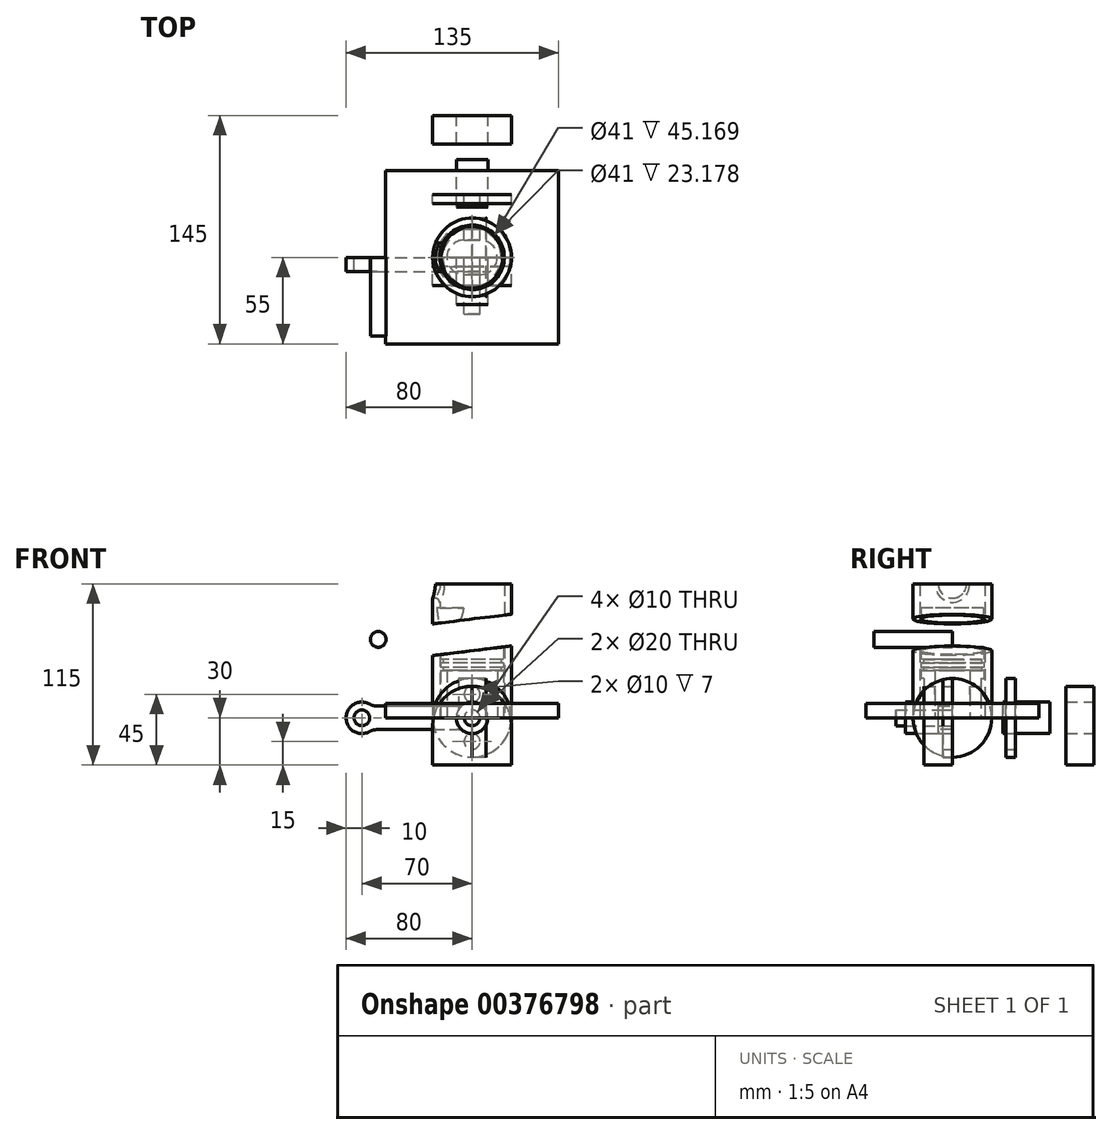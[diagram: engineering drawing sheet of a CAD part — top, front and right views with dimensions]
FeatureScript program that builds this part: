
annotation { "Feature Type Name" : "Feature", "Feature Type Description" : "" }
export const myFeature = defineFeature(function(context is Context, id is Id, definition is map)
    precondition{}
    {
        {
            var Q0;
            Q0=qCreatedBy(makeId("Front.planeOp"),FACE);
            var sketch = newSketch(context, id + "F0", { "sketchPlane" : qUnion([Q0])});
            skCircle(sketch, "E0", {"center": v(0, 0) * mm, "radius": 25 * mm});
            skCircle(sketch, "E1", {"center": v(0, -15) * mm, "radius": 5 * mm});
            skSolve(sketch);
        }
        {
            var Q0;
            Q0 = qSketchRegion(id + "F0", true);
            extrude(context, id + "F1", {"entities" : qUnion([Q0]), "depth" : 6 * mm});
        }
        {
            var Q0;
            Q0=makeQuery(id+"F1.opExtrude","SWEPT_BODY",BODY,{"disambiguationData":[OSD([sQuery(id+"F0.wireOp",EDGE,"E0"),sQuery(id+"F0.wireOp",EDGE,"E1")])]});
            transform(context, id + "F2", {"entities" : qUnion([Q0]), "transformType" : TransformType.TRANSLATION_3D, "dx" : 0 * mm, "dy" : 40 * mm, "dz" : 0 * mm, "makeCopy" : true});
        }
        {
            var Q0;
            Q0=qCreatedBy(makeId("Front.planeOp"),FACE);
            var sketch = newSketch(context, id + "F3", { "sketchPlane" : qUnion([Q0])});
            skCircle(sketch, "E2", {"center": v(-59.58, 49.8) * mm, "radius": 5 * mm});
            skSolve(sketch);
        }
        {
            var Q0;
            Q0=makeQuery(id+"F3.imprint","IMPRINT",FACE,{"disambiguationData":[TD([[makeQuery(id+"F3.imprint","IMPRINT",EDGE,{"derivedFrom":sQuery(id+"F3.wireOp",EDGE,"E2")}),1.0]])]});
            extrude(context, id + "F4", {"entities" : qUnion([Q0]), "depth" : 50 * mm});
        }
        {
            var Q0;
            Q0=qCreatedBy(makeId("Front.planeOp"),FACE);
            var sketch = newSketch(context, id + "F5", { "sketchPlane" : qUnion([Q0])});
            skCircle(sketch, "E3", {"center": v(0, 0) * mm, "radius": 10 * mm});
            skCircle(sketch, "E4", {"center": v(-70, 0) * mm, "radius": 10 * mm});
            skLineSegment(sketch, "E5", {"start": v(-70, 0) * mm, "end": v(0, 0) * mm, "construction": true});
            skLineSegment(sketch, "E6", {"start": v(-63.39, 7.5) * mm, "end": v(-6.61, 7.5) * mm});
            skLineSegment(sketch, "E7.MirrorCS", {"start": v(-63.39, -7.5) * mm, "end": v(-6.61, -7.5) * mm});
            skCircle(sketch, "E8", {"center": v(-70, 0) * mm, "radius": 5 * mm});
            skCircle(sketch, "E9", {"center": v(0, 0) * mm, "radius": 5 * mm});
            skSolve(sketch);
        }
        {
            var Q0;
            Q0 = qSketchRegion(id + "F5", true);
            extrude(context, id + "F6", {"entities" : qUnion([Q0]), "depth" : 9 * mm});
        }
        {
            var Q0;
            Q0=makeQuery(id+"F6.opExtrude","SWEPT_EDGE",EDGE,{"disambiguationData":[OSD([sQuery(id+"F5.wireOp",EDGE,"E4"),sQuery(id+"F5.wireOp",EDGE,"E6")])]});
            var Q1;
            Q1=makeQuery(id+"F6.opExtrude","SWEPT_EDGE",EDGE,{"disambiguationData":[OSD([sQuery(id+"F5.wireOp",EDGE,"E4"),sQuery(id+"F5.wireOp",EDGE,"E7.MirrorCS")])]});
            fillet(context, id + "F7", {"entities" : qUnion([Q0, Q1]), "radius" : 10 * mm, "tangentPropagation" : true, "allowEdgeOverflow" : false});
        }
        {
            var Q0;
            Q0=makeQuery(id+"F6.opExtrude","SWEPT_EDGE",EDGE,{"disambiguationData":[OSD([sQuery(id+"F5.wireOp",EDGE,"E3"),sQuery(id+"F5.wireOp",EDGE,"E6")])]});
            var Q1;
            Q1=makeQuery(id+"F6.opExtrude","SWEPT_EDGE",EDGE,{"disambiguationData":[OSD([sQuery(id+"F5.wireOp",EDGE,"E3"),sQuery(id+"F5.wireOp",EDGE,"E7.MirrorCS")])]});
            fillet(context, id + "F8", {"entities" : qUnion([Q0, Q1]), "radius" : 10 * mm, "tangentPropagation" : true, "allowEdgeOverflow" : false});
        }
        {
            var Q0;
            Q0=qCreatedBy(makeId("Top.planeOp"),FACE);
            var sketch = newSketch(context, id + "F9", { "sketchPlane" : qUnion([Q0])});
            skCircle(sketch, "E10", {"center": v(0, 0) * mm, "radius": 20 * mm});
            skSolve(sketch);
        }
        {
            var Q0;
            Q0 = qSketchRegion(id + "F9", true);
            extrude(context, id + "F10", {"entities" : qUnion([Q0]), "depth" : 40 * mm});
        }
        {
            var Q0;
            Q0=qCreatedBy(makeId("Top.planeOp"),FACE);
            var sketch = newSketch(context, id + "F11", { "sketchPlane" : qUnion([Q0])});
            skCircle(sketch, "E11", {"center": v(0, 0) * mm, "radius": 11 * mm});
            skCircle(sketch, "E12", {"center": v(10, 0) * mm, "radius": 11 * mm});
            skLineSegment(sketch, "E13", {"start": v(0, -11) * mm, "end": v(10, -11) * mm});
            skLineSegment(sketch, "E14.MirrorCS", {"start": v(0, 11) * mm, "end": v(10, 11) * mm});
            skSolve(sketch);
        }
        {
            var Q0;
            {var subQ0=sQuery(id+"F11.wireOp",EDGE,"E14.MirrorCS");Q0=makeQuery(id+"F11.imprint","IMPRINT",FACE,{"disambiguationData":[TD([[makeQuery(id+"F11.imprint","IMPRINT",EDGE,{"derivedFrom":subQ0}),-1.0]])]});}
            var Q1;
            {var subQ0=sQuery(id+"F11.wireOp",EDGE,"E13");Q1=makeQuery(id+"F11.imprint","IMPRINT",FACE,{"disambiguationData":[TD([[makeQuery(id+"F11.imprint","IMPRINT",EDGE,{"derivedFrom":subQ0}),1.0]])]});}
            var Q2;
            {var subQ0=sQuery(id+"F11.wireOp",EDGE,"E12");var subQ1=sQuery(id+"F11.wireOp",EDGE,"E11");var subQ2=makeQuery(id+"F11.imprint","INTERSECT",VERTEX,{"disambiguationData":[OD(0.0)],"derivedFrom":[subQ1,subQ0]});Q2=makeQuery(id+"F11.imprint","IMPRINT",FACE,{"disambiguationData":[TD([[makeQuery(id+"F11.imprint","IMPRINT",EDGE,{"disambiguationData":[TD([[subQ2,1.0]])],"derivedFrom":subQ1}),1.0]])]});}
            var Q3;
            {var subQ0=sQuery(id+"F11.wireOp",EDGE,"E12");var subQ1=sQuery(id+"F11.wireOp",EDGE,"E11");var subQ2=makeQuery(id+"F11.imprint","INTERSECT",VERTEX,{"disambiguationData":[OD(0.0)],"derivedFrom":[subQ1,subQ0]});Q3=makeQuery(id+"F11.imprint","IMPRINT",FACE,{"disambiguationData":[TD([[makeQuery(id+"F11.imprint","IMPRINT",EDGE,{"disambiguationData":[TD([[subQ2,1.0]])],"derivedFrom":subQ1}),-1.0]])]});}
            var Q4;
            {var subQ0=sQuery(id+"F11.wireOp",EDGE,"E11");var subQ1=makeQuery(id+"F11.imprint","INTERSECT",VERTEX,{"derivedFrom":[subQ0,sQuery(id+"F11.wireOp",EDGE,"E14.MirrorCS")]});Q4=makeQuery(id+"F11.imprint","IMPRINT",FACE,{"disambiguationData":[TD([[makeQuery(id+"F11.imprint","IMPRINT",EDGE,{"disambiguationData":[TD([[subQ1,1.0]])],"derivedFrom":subQ0}),1.0]])]});}
            extrude(context, id + "F12", {"entities" : qUnion([Q0, Q1, Q2, Q3, Q4]), "depth" : 30 * mm});
        }
        {
            var Q0;
            Q0=makeQuery(id+"F12.opExtrude","SWEPT_BODY",BODY,{"disambiguationData":[OSD([sQuery(id+"F11.wireOp",EDGE,"E11"),sQuery(id+"F11.wireOp",EDGE,"E12"),sQuery(id+"F11.wireOp",EDGE,"E13"),sQuery(id+"F11.wireOp",EDGE,"E14.MirrorCS")])]});
            var Q1;
            Q1=qCreatedBy(makeId("Right.planeOp"),FACE);
            transform(context, id + "F13", {"entities" : qUnion([Q0]), "transformType" : TransformType.TRANSLATION_DISTANCE, "transformDirection" : qUnion([Q1]), "distance" : 5 * mm, "oppositeDirection" : true, "makeCopy" : false});
        }
        {
            var Q0;
            Q0=makeQuery(id+"F12.opExtrude","SWEPT_BODY",BODY,{"disambiguationData":[OSD([sQuery(id+"F11.wireOp",EDGE,"E11"),sQuery(id+"F11.wireOp",EDGE,"E12"),sQuery(id+"F11.wireOp",EDGE,"E13"),sQuery(id+"F11.wireOp",EDGE,"E14.MirrorCS")])]});
            var Q1;
            Q1=makeQuery(id+"F10.opExtrude","SWEPT_BODY",BODY,{"disambiguationData":[OSD([sQuery(id+"F9.wireOp",EDGE,"E10")])]});
            booleanBodies(context, id + "F14", {"operationType" : BooleanOperationType.SUBTRACTION, "tools" : qUnion([Q0]), "targets" : qUnion([Q1])});
        }
        {
            var Q0;
            Q0=qCreatedBy(makeId("Top.planeOp"),FACE);
            var sketch = newSketch(context, id + "F15", { "sketchPlane" : qUnion([Q0])});
            skLineSegment(sketch, "E15.bottom", {"start": v(-45, 18) * mm, "end": v(45, 18) * mm});
            skLineSegment(sketch, "E15.top", {"start": v(-45, -18) * mm, "end": v(45, -18) * mm});
            skLineSegment(sketch, "E15.left", {"start": v(-45, 18) * mm, "end": v(-45, -18) * mm});
            skLineSegment(sketch, "E15.right", {"start": v(45, 18) * mm, "end": v(45, -18) * mm});
            skPoint(sketch, "E15.middle", {"position": v(0, 0) * mm});
            skSolve(sketch);
        }
        {
            var Q0;
            Q0 = qSketchRegion(id + "F15", true);
            extrude(context, id + "F16", {"entities" : qUnion([Q0]), "depth" : 35 * mm});
        }
        {
            var Q0;
            Q0=qCreatedBy(makeId("Top.planeOp"),FACE);
            var sketch = newSketch(context, id + "F17", { "sketchPlane" : qUnion([Q0])});
            skLineSegment(sketch, "E16.bottom", {"start": v(-50, 23) * mm, "end": v(50, 23) * mm});
            skLineSegment(sketch, "E16.top", {"start": v(-50, -23) * mm, "end": v(50, -23) * mm});
            skLineSegment(sketch, "E16.left", {"start": v(-50, 23) * mm, "end": v(-50, -23) * mm});
            skLineSegment(sketch, "E16.right", {"start": v(50, 23) * mm, "end": v(50, -23) * mm});
            skPoint(sketch, "E16.middle", {"position": v(0, 0) * mm});
            skSolve(sketch);
        }
        {
            var Q0;
            Q0 = qSketchRegion(id + "F17", true);
            extrude(context, id + "F18", {"entities" : qUnion([Q0]), "depth" : 25 * mm});
        }
        {
            var Q0;
            Q0=makeQuery(id+"F16.opExtrude","SWEPT_BODY",BODY,{"disambiguationData":[OSD([sQuery(id+"F15.wireOp",EDGE,"E15.bottom"),sQuery(id+"F15.wireOp",EDGE,"E15.top"),sQuery(id+"F15.wireOp",EDGE,"E15.left"),sQuery(id+"F15.wireOp",EDGE,"E15.right")])]});
            var Q1;
            Q1=makeQuery(id+"F18.opExtrude","SWEPT_BODY",BODY,{"disambiguationData":[OSD([sQuery(id+"F17.wireOp",EDGE,"E16.bottom"),sQuery(id+"F17.wireOp",EDGE,"E16.top"),sQuery(id+"F17.wireOp",EDGE,"E16.left"),sQuery(id+"F17.wireOp",EDGE,"E16.right")])]});
            booleanBodies(context, id + "F19", {"operationType" : BooleanOperationType.SUBTRACTION, "tools" : qUnion([Q0]), "targets" : qUnion([Q1])});
        }
        {
            var Q0;
            Q0=makeQuery(id+"F18.opExtrude","SWEPT_BODY",BODY,{"disambiguationData":[OSD([sQuery(id+"F17.wireOp",EDGE,"E16.bottom"),sQuery(id+"F17.wireOp",EDGE,"E16.top"),sQuery(id+"F17.wireOp",EDGE,"E16.left"),sQuery(id+"F17.wireOp",EDGE,"E16.right")])]});
            var Q1;
            Q1=makeQuery(id+"F10.opExtrude","SWEPT_BODY",BODY,{"disambiguationData":[OSD([sQuery(id+"F9.wireOp",EDGE,"E10")])]});
            booleanBodies(context, id + "F20", {"operationType" : BooleanOperationType.SUBTRACTION, "tools" : qUnion([Q0]), "targets" : qUnion([Q1])});
        }
        {
            var Q0;
            Q0=makeQuery(id+"F20.opBoolean","COPY",FACE,{"derivedFrom":makeQuery(id+"F19.opBoolean","COPY",FACE,{"derivedFrom":makeQuery(id+"F16.opExtrude","SWEPT_FACE",FACE,{"disambiguationData":[OSD([sQuery(id+"F15.wireOp",EDGE,"E15.top")])]})})});
            var sketch = newSketch(context, id + "F21", { "sketchPlane" : qUnion([Q0])});
            skCircle(sketch, "E17", {"center": v(0, 15) * mm, "radius": 5 * mm});
            skSolve(sketch);
        }
        {
            var Q0;
            Q0=makeQuery(id+"F21.imprint","IMPRINT",FACE,{"disambiguationData":[TD([[makeQuery(id+"F21.imprint","IMPRINT",EDGE,{"derivedFrom":sQuery(id+"F21.wireOp",EDGE,"E17")}),1.0]])]});
            extrude(context, id + "F22", {"entities" : qUnion([Q0]), "depth" : 45 * mm});
        }
        {
            var Q0;
            Q0=makeQuery(id+"F22.opExtrude","SWEPT_BODY",BODY,{"disambiguationData":[OSD([sQuery(id+"F21.wireOp",EDGE,"E17")])]});
            var Q1;
            Q1=qCreatedBy(makeId("Front.planeOp"),FACE);
            transform(context, id + "F23", {"entities" : qUnion([Q0]), "transformType" : TransformType.TRANSLATION_DISTANCE, "transformDirection" : qUnion([Q1]), "distance" : 41 * mm, "oppositeDirection" : true, "makeCopy" : false});
        }
        {
            var Q0;
            Q0=makeQuery(id+"F22.opExtrude","SWEPT_BODY",BODY,{"disambiguationData":[OSD([sQuery(id+"F21.wireOp",EDGE,"E17")])]});
            var Q1;
            Q1=makeQuery(id+"F10.opExtrude","SWEPT_BODY",BODY,{"disambiguationData":[OSD([sQuery(id+"F9.wireOp",EDGE,"E10")])]});
            booleanBodies(context, id + "F24", {"operationType" : BooleanOperationType.SUBTRACTION, "tools" : qUnion([Q0]), "targets" : qUnion([Q1])});
        }
        {
            var Q0;
            Q0=qCreatedBy(makeId("Top.planeOp"),FACE);
            var sketch = newSketch(context, id + "F25", { "sketchPlane" : qUnion([Q0])});
            skCircle(sketch, "E18", {"center": v(0, 0) * mm, "radius": 25 * mm});
            skCircle(sketch, "E19", {"center": v(0, 0) * mm, "radius": 18.5 * mm});
            skSolve(sketch);
        }
        {
            var Q0;
            Q0 = qSketchRegion(id + "F25", true);
            extrude(context, id + "F26", {"entities" : qUnion([Q0]), "depth" : 2 * mm});
        }
        {
            var Q0;
            Q0=makeQuery(id+"F26.opExtrude","SWEPT_BODY",BODY,{"disambiguationData":[OSD([sQuery(id+"F25.wireOp",EDGE,"E18"),sQuery(id+"F25.wireOp",EDGE,"E19")])]});
            var Q1;
            Q1=qCreatedBy(makeId("Top.planeOp"),FACE);
            transform(context, id + "F27", {"entities" : qUnion([Q0]), "transformType" : TransformType.TRANSLATION_DISTANCE, "transformDirection" : qUnion([Q1]), "distance" : 30 * mm, "makeCopy" : false});
        }
        {
            var Q0;
            Q0=makeQuery(id+"F26.opExtrude","SWEPT_BODY",BODY,{"disambiguationData":[OSD([sQuery(id+"F25.wireOp",EDGE,"E18"),sQuery(id+"F25.wireOp",EDGE,"E19")])]});
            transform(context, id + "F28", {"entities" : qUnion([Q0]), "transformType" : TransformType.TRANSLATION_3D, "dx" : 0 * mm, "dy" : 0 * mm, "dz" : 5 * mm, "makeCopy" : true});
        }
        {
            var Q0;
            Q0=makeQuery(id+"F28.opPattern","COPY",BODY,{"derivedFrom":makeQuery(id+"F26.opExtrude","SWEPT_BODY",BODY,{"disambiguationData":[OSD([sQuery(id+"F25.wireOp",EDGE,"E18"),sQuery(id+"F25.wireOp",EDGE,"E19")])]}),"instanceName":"1"});
            var Q1;
            Q1=makeQuery(id+"F26.opExtrude","SWEPT_BODY",BODY,{"disambiguationData":[OSD([sQuery(id+"F25.wireOp",EDGE,"E18"),sQuery(id+"F25.wireOp",EDGE,"E19")])]});
            var Q2;
            Q2=makeQuery(id+"F10.opExtrude","SWEPT_BODY",BODY,{"disambiguationData":[OSD([sQuery(id+"F9.wireOp",EDGE,"E10")])]});
            booleanBodies(context, id + "F29", {"operationType" : BooleanOperationType.SUBTRACTION, "tools" : qUnion([Q0, Q1]), "targets" : qUnion([Q2])});
        }
        {
            var Q0;
            Q0=qCreatedBy(makeId("Front.planeOp"),FACE);
            var sketch = newSketch(context, id + "F30", { "sketchPlane" : qUnion([Q0])});
            skCircle(sketch, "E20", {"center": v(0, 0) * mm, "radius": 5 * mm});
            skSolve(sketch);
        }
        {
            var Q0;
            Q0 = qSketchRegion(id + "F30", true);
            extrude(context, id + "F31", {"entities" : qUnion([Q0]), "depth" : 36 * mm});
        }
        {
            var Q0;
            Q0=qCreatedBy(makeId("Top.planeOp"),FACE);
            var sketch = newSketch(context, id + "F32", { "sketchPlane" : qUnion([Q0])});
            skCircle(sketch, "E21", {"center": v(0, 0) * mm, "radius": 25 * mm});
            skCircle(sketch, "E22", {"center": v(0, 0) * mm, "radius": 20.5 * mm});
            skSolve(sketch);
        }
        {
            var Q0;
            Q0 = qSketchRegion(id + "F32", true);
            extrude(context, id + "F33", {"entities" : qUnion([Q0]), "depth" : 85 * mm});
        }
        {
            var Q0;
            Q0=qCreatedBy(makeId("Front.planeOp"),FACE);
            var sketch = newSketch(context, id + "F34", { "sketchPlane" : qUnion([Q0])});
            skCircle(sketch, "E23", {"center": v(0, 0) * mm, "radius": 10 * mm});
            skSolve(sketch);
        }
        {
            var Q0;
            Q0=makeQuery(id+"F34.imprint","IMPRINT",FACE,{"disambiguationData":[TD([[makeQuery(id+"F34.imprint","IMPRINT",EDGE,{"derivedFrom":sQuery(id+"F34.wireOp",EDGE,"E23")}),1.0]])]});
            extrude(context, id + "F35", {"entities" : qUnion([Q0]), "depth" : 30 * mm});
        }
        {
            var Q0;
            Q0=makeQuery(id+"F35.opExtrude","SWEPT_BODY",BODY,{"disambiguationData":[OSD([sQuery(id+"F34.wireOp",EDGE,"E23")])]});
            transform(context, id + "F36", {"entities" : qUnion([Q0]), "transformType" : TransformType.TRANSLATION_3D, "dx" : 0 * mm, "dy" : 62 * mm, "dz" : 0 * mm, "makeCopy" : true});
        }
        {
            var Q0;
            Q0=qCreatedBy(makeId("Front.planeOp"),FACE);
            var sketch = newSketch(context, id + "F37", { "sketchPlane" : qUnion([Q0])});
            skCircle(sketch, "E24", {"center": v(0, 0) * mm, "radius": 10 * mm});
            skLineSegment(sketch, "E25.bottom", {"start": v(0, 20) * mm, "end": v(0, 20) * mm});
            skLineSegment(sketch, "E25.top", {"start": v(-25, -30) * mm, "end": v(25, -30) * mm});
            skLineSegment(sketch, "E25.left", {"start": v(-25, -5) * mm, "end": v(-25, -30) * mm});
            skLineSegment(sketch, "E25.right", {"start": v(25, -5) * mm, "end": v(25, -30) * mm});
            skPoint(sketch, "E26.visualSharp", {"position": v(-25, 20) * mm});
            skArc(sketch, "E26.filletArc", {"start": v(0, 20) * mm, "mid": v(-17.68, 12.68) * mm, "end": v(-25, -5) * mm});
            skPoint(sketch, "E27.visualSharp", {"position": v(25, 20) * mm});
            skArc(sketch, "E27.filletArc", {"start": v(25, -5) * mm, "mid": v(17.68, 12.68) * mm, "end": v(0, 20) * mm});
            skSolve(sketch);
        }
        {
            var Q0;
            Q0 = qSketchRegion(id + "F37", true);
            extrude(context, id + "F38", {"entities" : qUnion([Q0]), "depth" : 18 * mm});
        }
        {
            var Q0;
            Q0=makeQuery(id+"F38.opExtrude","SWEPT_BODY",BODY,{"disambiguationData":[OSD([sQuery(id+"F37.wireOp",EDGE,"E24"),sQuery(id+"F37.wireOp",EDGE,"E25.top"),sQuery(id+"F37.wireOp",EDGE,"E25.left"),sQuery(id+"F37.wireOp",EDGE,"E25.right"),sQuery(id+"F37.wireOp",EDGE,"E26.filletArc"),sQuery(id+"F37.wireOp",EDGE,"E27.filletArc")])]});
            transform(context, id + "F39", {"entities" : qUnion([Q0]), "transformType" : TransformType.TRANSLATION_3D, "dx" : 0 * mm, "dy" : 90 * mm, "dz" : 0 * mm, "makeCopy" : true});
        }
        {
            var Q0;
            Q0=qCreatedBy(makeId("Top.planeOp"),FACE);
            var sketch = newSketch(context, id + "F40", { "sketchPlane" : qUnion([Q0])});
            skLineSegment(sketch, "E28.bottom", {"start": v(-55, 55) * mm, "end": v(55, 55) * mm});
            skLineSegment(sketch, "E28.top", {"start": v(-55, -55) * mm, "end": v(55, -55) * mm});
            skLineSegment(sketch, "E28.left", {"start": v(-55, 55) * mm, "end": v(-55, -55) * mm});
            skLineSegment(sketch, "E28.right", {"start": v(55, 55) * mm, "end": v(55, -55) * mm});
            skSolve(sketch);
        }
        {
            var Q0;
            Q0 = qSketchRegion(id + "F40", true);
            extrude(context, id + "F41", {"entities" : qUnion([Q0]), "depth" : 9 * mm});
        }
        {
            var Q0;
            Q0=qCreatedBy(makeId("Right.planeOp"),FACE);
            var sketch = newSketch(context, id + "F42", { "sketchPlane" : qUnion([Q0])});
            skCircle(sketch, "E29", {"center": v(0, 0) * mm, "radius": 25 * mm});
            skSolve(sketch);
        }
        {
            var Q0;
            Q0=makeQuery(id+"F42.imprint","IMPRINT",FACE,{"disambiguationData":[TD([[makeQuery(id+"F42.imprint","IMPRINT",EDGE,{"derivedFrom":sQuery(id+"F42.wireOp",EDGE,"E29")}),1.0]])]});
            extrude(context, id + "F43", {"entities" : qUnion([Q0]), "depth" : 9 * mm});
        }
        {
            var Q0;
            Q0=qCreatedBy(makeId("Right.planeOp"),FACE);
            var sketch = newSketch(context, id + "F44", { "sketchPlane" : qUnion([Q0])});
            skCircle(sketch, "E30", {"center": v(0, 85) * mm, "radius": 9 * mm});
            skSolve(sketch);
        }
        {
            var Q0;
            Q0 = qSketchRegion(id + "F44", true);
            extrude(context, id + "F45", {"entities" : qUnion([Q0]), "operationType" : NewBodyOperationType.REMOVE, "oppositeDirection" : true, "depth" : 30 * mm});
        }
        {
            var Q0;
            Q0=makeQuery(id+"F45.boolean.opBoolean","INTERSECT",EDGE,{"derivedFrom":[makeQuery(id+"F33.opExtrude","SWEPT_FACE",FACE,{"disambiguationData":[OSD([sQuery(id+"F32.wireOp",EDGE,"E22")])]}),makeQuery(id+"F45.opExtrude","SWEPT_FACE",FACE,{"disambiguationData":[OSD([sQuery(id+"F44.wireOp",EDGE,"E30")])]})]});
            fillet(context, id + "F46", {"entities" : qUnion([Q0]), "radius" : 3 * mm, "allowEdgeOverflow" : false});
        }
        {
            var Q0;
            Q0=makeQuery(id+"F10.opExtrude","CAP_FACE",FACE,{"disambiguationData":[OSD([sQuery(id+"F9.wireOp",EDGE,"E10")])],"isStart":false});
            var sketch = newSketch(context, id + "F47", { "sketchPlane" : qUnion([Q0])});
            skCircle(sketch, "E31", {"center": v(0, 0) * mm, "radius": 20 * mm});
            skSolve(sketch);
        }
        {
            var Q0;
            Q0 = qSketchRegion(id + "F47", true);
            extrude(context, id + "F48", {"entities" : qUnion([Q0]), "operationType" : NewBodyOperationType.ADD, "depth" : 10 * mm});
        }
        {
            var Q0;
            Q0=qCreatedBy(makeId("Front.planeOp"),FACE);
            var sketch = newSketch(context, id + "F49", { "sketchPlane" : qUnion([Q0])});
            skLineSegment(sketch, "E32", {"start": v(-21.32, 40) * mm, "end": v(22.43, 45.37) * mm, "construction": true});
            skSolve(sketch);
        }
        {
            var Q0;
            Q0=sQuery(id+"F49.wireOp",EDGE,"E32");
            cPlane(context, id + "F50", {"entities" : qUnion([Q0]), "cplaneType" : CPlaneType.LINE_ANGLE, "offset" : 0 * mm, "angle" : 90 * degree, "width" : 150 * mm, "height" : 150 * mm});
        }
        {
            var Q0;
            Q0=qCreatedBy(id+"F50.planeOp",FACE);
            var sketch = newSketch(context, id + "F51", { "sketchPlane" : qUnion([Q0])});
            skLineSegment(sketch, "E33.bottom", {"start": v(-24.97, 28.66) * mm, "end": v(34.4, 28.66) * mm});
            skLineSegment(sketch, "E33.top", {"start": v(-24.97, -28.66) * mm, "end": v(34.4, -28.66) * mm});
            skLineSegment(sketch, "E33.left", {"start": v(-24.97, 28.66) * mm, "end": v(-24.97, -28.66) * mm});
            skLineSegment(sketch, "E33.right", {"start": v(34.4, 28.66) * mm, "end": v(34.4, -28.66) * mm});
            skPoint(sketch, "E33.middle", {"position": v(4.7, 0) * mm});
            skSolve(sketch);
        }
        {
            var Q0;
            Q0=makeQuery(id+"F51.imprint","IMPRINT",FACE,{"disambiguationData":[TD([[makeQuery(id+"F51.imprint","IMPRINT",EDGE,{"derivedFrom":sQuery(id+"F51.wireOp",EDGE,"E33.bottom")}),-1.0]])]});
            var Q1;
            Q1=makeQuery(id+"F48.opExtrude","CAP_FACE",FACE,{"disambiguationData":[OSD([sQuery(id+"F47.wireOp",EDGE,"E31")])],"isStart":false});
            extrude(context, id + "F52", {"entities" : qUnion([Q0, Q1]), "operationType" : NewBodyOperationType.REMOVE, "depth" : 20 * mm});
        }
    });
